# Revit family: 3079102 Sylvania_Clio LED_Surface Mounted
name_source: partatom
category: Lighting Fixtures
revit_build: Autodesk Revit 2017 (Build: 20190507_1515(x64)
units: mm (PartAtom-declared; Revit-internal decimal feet)

## family parameters
Cut with Voids When Loaded = No
Host = Face
Light Source = Yes
OmniClass Number = 23.80.70.11.17
OmniClass Title = Specialized Lighting by Location or Use
Part Type = Normal
Room Calculation Point = No
Round Connector Dimension = Use Diameter
Shared = No

## types (2) — shared parameters
Apparent Load = 20 VA
Assembly Code = D5020200
Body Material = Polycarbonate_Sylvania_Clio LED_White
Color Filter = 16777215
Description = Clio LED is a new range of wall and
ceiling mounted ambient LED luminaires.
Thanks to its IP44 rating, the range can be
used in corridors, circulation spaces and
foyers or applicable zone 1 bathroom and
wet areas.
Clio LED benefits from a simple yet
robust design. It offers a uniform light
distribution whilst providing an ambient
halo lighting effect on the wall surface.
Clio LED allows for surface wiring and also
has loop-in loop-out capability, making it a
contractor’s first choice.
Diameter = 320 mm  [stored 1.04987 ft]
Difuser Material = Acrylic Glass_Sylvania_Clio LED_White
Dimming Lamp Color Temperature Shift = <None>
Drive Current = 300 mA
Electrical Protection = Class II
Height = 108 mm  [stored 0.354331 ft]
IK Rating = IK 04
IP Rating = IP 44
Lamp = 20W
Lamp Comments = Integrated LED
Life = 40 000h
Manufacturer = Feilo Sylvania
Product Family = CLIO LED
Product Page URL = http://www.sylvania-lighting.com
Radius = 160 mm  [stored 0.524934 ft]
Tilt Angle = -90.00°
URL = http://www.sylvania-lighting.com
Voltage = 230 V
Voltage Comments = UNV (Universal Voltage; 230-240 Volt)
zero-valued in all types: Default Elevation

## per-type parameters (varying)
| type | Catalog Number | Photometric Web File |
| CLIO 320 HO LED 20W WW EB | 3079101 CLIO 320 HO LED 20W WW EB | 3079101 20W 3000K.ies |
| CLIO 320 HO LED 20W NW EB | 3079102 CLIO 320 HO LED 20W WW EB | 3079102_Clio320HOLED4000K-180002.ies |

note: column(s) folded — value = type name in every type: Model

note: [stored X ft] marks values corroborated as IEEE doubles in the binary element streams (Revit-internal decimal feet)

## geometry (parser evidence)
native form markers: Sweep x2
no freeform markers — native parametric forms only
